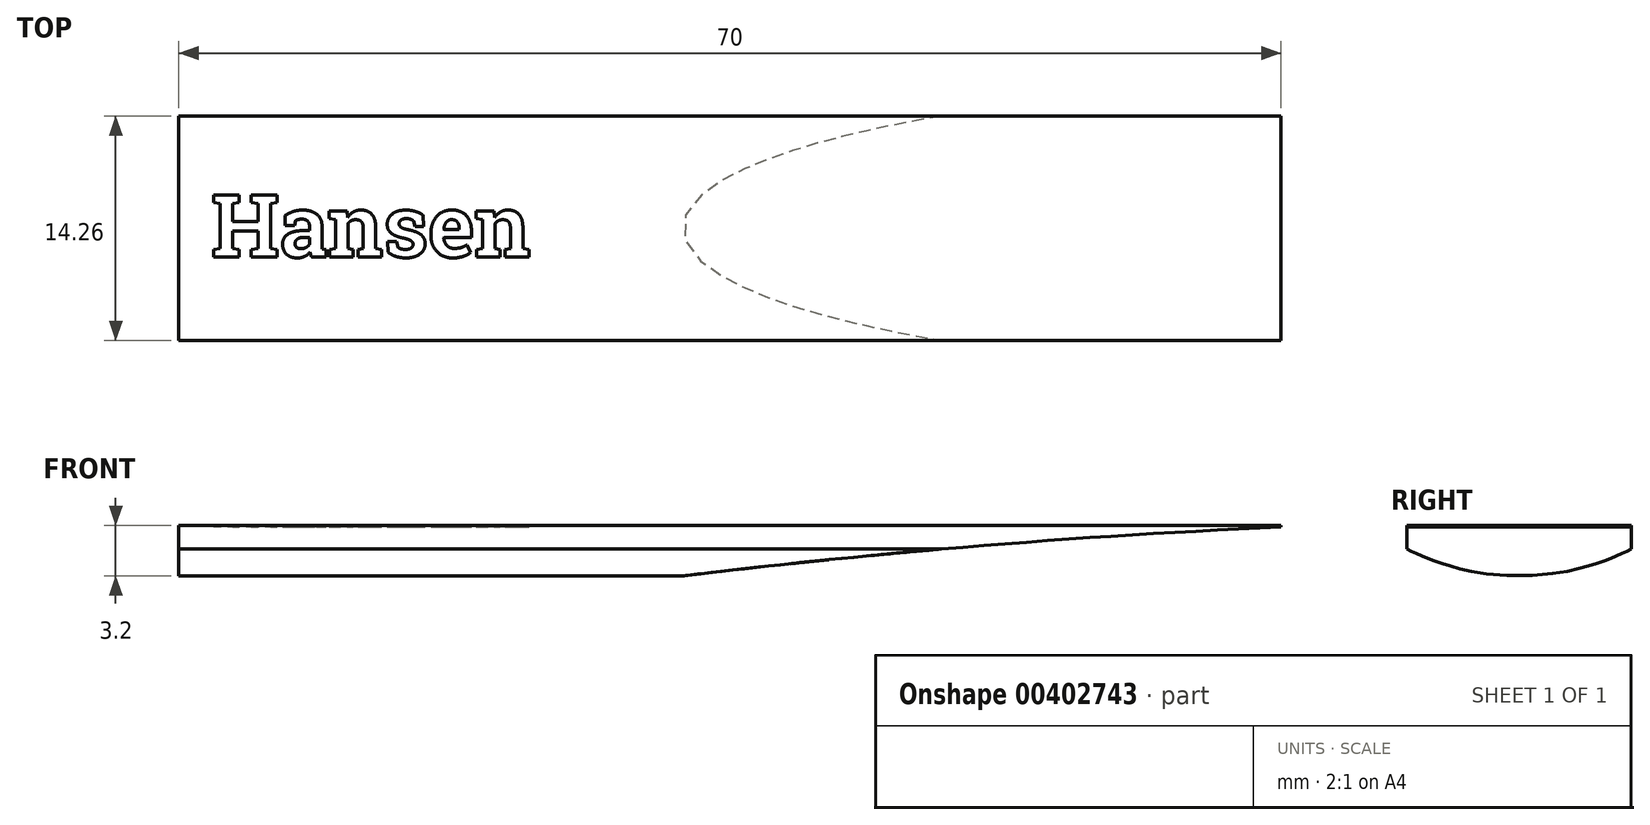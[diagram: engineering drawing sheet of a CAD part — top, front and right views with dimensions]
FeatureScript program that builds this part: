
annotation { "Feature Type Name" : "Feature", "Feature Type Description" : "" }
export const myFeature = defineFeature(function(context is Context, id is Id, definition is map)
    precondition{}
    {
        {
            var Q0;
            Q0=qCreatedBy(makeId("Right.planeOp"),FACE);
            var sketch = newSketch(context, id + "F0", { "sketchPlane" : qUnion([Q0])});
            skLineSegment(sketch, "E0", {"start": v(-7.13, 0) * mm, "end": v(7.13, 0) * mm});
            skLineSegment(sketch, "E1", {"start": v(7.12, 0) * mm, "end": v(7.12, -1.5) * mm});
            skLineSegment(sketch, "E2", {"start": v(-7.13, 0) * mm, "end": v(-7.13, -1.5) * mm});
            skArc(sketch, "E3", {"start": v(-7.13, -1.5) * mm, "mid": v(0, -3.2) * mm, "end": v(7.13, -1.5) * mm});
            skLineSegment(sketch, "E4", {"start": v(0, 0) * mm, "end": v(0, -3.2) * mm});
            skSolve(sketch);
        }
        {
            var Q0;
            {var subQ0=sQuery(id+"F0.wireOp",EDGE,"E2");Q0=makeQuery(id+"F0.imprint","IMPRINT",FACE,{"disambiguationData":[TD([[makeQuery(id+"F0.imprint","IMPRINT",EDGE,{"derivedFrom":subQ0}),1.0]])]});}
            var Q1;
            {var subQ0=sQuery(id+"F0.wireOp",EDGE,"E1");Q1=makeQuery(id+"F0.imprint","IMPRINT",FACE,{"disambiguationData":[TD([[makeQuery(id+"F0.imprint","IMPRINT",EDGE,{"derivedFrom":subQ0}),-1.0]])]});}
            extrude(context, id + "F1", {"entities" : qUnion([Q0, Q1]), "endBound" : BoundingType.SYMMETRIC, "depth" : 70 * mm});
        }
        {
            var Q0;
            Q0=qCreatedBy(makeId("Front.planeOp"),FACE);
            var sketch = newSketch(context, id + "F2", { "sketchPlane" : qUnion([Q0])});
            skLineSegment(sketch, "E5", {"start": v(0, 0) * mm, "end": v(-35, 0) * mm});
            skLineSegment(sketch, "E6", {"start": v(-35, 0) * mm, "end": v(-3, 0) * mm});
            skLineSegment(sketch, "E7", {"start": v(-3, 0) * mm, "end": v(-3, -3.2) * mm});
            skLineSegment(sketch, "E8", {"start": v(-3, -3.2) * mm, "end": v(-3, -3.97) * mm});
            skLineSegment(sketch, "E9", {"start": v(-3, 0) * mm, "end": v(35, 0) * mm});
            skLineSegment(sketch, "E10", {"start": v(35, 0) * mm, "end": v(35, -0.1) * mm});
            skArc(sketch, "E11", {"start": v(35, -0.1) * mm, "mid": v(15.97, -1.29) * mm, "end": v(-3, -3.2) * mm});
            skLineSegment(sketch, "E12", {"start": v(-3, -3.97) * mm, "end": v(39.89, -8) * mm});
            skLineSegment(sketch, "E13", {"start": v(39.89, -8) * mm, "end": v(41.68, -2.3) * mm});
            skLineSegment(sketch, "E14", {"start": v(41.68, -2.3) * mm, "end": v(35, -0.1) * mm});
            skSolve(sketch);
        }
        {
            var Q0;
            Q0=makeQuery(id+"F2.imprint","IMPRINT",FACE,{"disambiguationData":[TD([[makeQuery(id+"F2.imprint","IMPRINT",EDGE,{"derivedFrom":sQuery(id+"F2.wireOp",EDGE,"E8")}),1.0]])]});
            extrude(context, id + "F3", {"entities" : qUnion([Q0]), "operationType" : NewBodyOperationType.REMOVE, "endBound" : BoundingType.SYMMETRIC, "oppositeDirection" : true, "depth" : 30 * mm});
        }
        {
            var Q0;
            Q0=makeQuery(id+"F1.opExtrude","SWEPT_FACE",FACE,{"disambiguationData":[OSD([sQuery(id+"F0.wireOp",EDGE,"E0")])]});
            var sketch = newSketch(context, id + "F4", { "sketchPlane" : qUnion([Q0])});
            skText(sketch, "E15", { "text": "Hansen", "fontName": "RobotoSlab-Bold.ttf"});
            const initialGuessF4  = {"E15": [-0.03295, -0.00183, 1, 0, 0.004]};
            skSetInitialGuess(sketch, initialGuessF4);
            skSolve(sketch);
        }
        {
            var Q0;
            Q0 = qSketchRegion(id + "F4", true);
            extrude(context, id + "F5", {"entities" : qUnion([Q0]), "operationType" : NewBodyOperationType.REMOVE, "oppositeDirection" : true, "depth" : 0.1 * mm});
        }
    });
